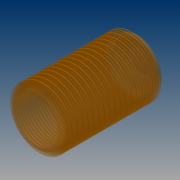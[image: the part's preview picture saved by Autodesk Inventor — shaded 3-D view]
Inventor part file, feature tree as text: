
AUTODESK INVENTOR PART (.ipt)
format: ipt  version: 2015 (Build 190159000, 159)  size: 459,264 bytes
history: native  units: mm
features: revolve x1, sketch x1
ambient origin geometry x8: Origin, YZ Plane, XZ Plane, XY Plane, X Axis, Y Axis, Z Axis, Center Point
bodies: Solid1 (feature_tree)
feature tree (2):
  revolve  "Revolution1"  [1 undecoded]
  sketch  "Sketch1"  dims[d34=40.0mm d36=20.0mm d37=10.0mm d38=5.0mm d39=10.0mm d40=2.0mm d41=10.0mm d42=10.0mm d43=2.0mm d44=10.0mm d45=2.0mm d46=10.0mm d47=2.0mm d48=10.0mm d49=2.0mm d50=10.0mm d51=2.0mm d52=10.0mm d53=2.0mm d54=10.0mm d55=2.0mm d56=10.0mm d57=2.0mm d59=2.0mm d62=3.0mm d63=3.0mm d64=3.0mm d65=3.0mm d66=3.0mm d67=3.0mm d68=3.0mm d69=3.0mm d70=3.0mm d72=90.0deg d73=2.0mm d74=2.0mm d75=2.0mm d76=2.0mm d77=2.0mm d78=2.0mm d79=2.0mm d80=2.0mm d81=3.0mm d82=10.0mm d83=3.0mm d84=3.0mm d85=3.0mm d86=3.0mm d87=3.0mm d88=3.0mm d89=3.0mm d90=195.0mm d91=2.0mm d92=2.0mm d93=2.0mm d94=2.0mm d95=2.0mm d96=2.0mm d97=2.0mm d98=2.0mm d99=2.0mm d101=3.0mm d102=3.0mm d103=3.0mm d104=3.0mm d105=3.0mm d106=3.0mm d107=3.0mm d108=3.0mm d109=3.0mm d110=2.0mm d111=2.0mm d112=2.0mm d113=3.0mm d114=3.0mm d115=3.0mm d116=2.0mm d117=2.0mm d118=2.0mm d119=2.0mm d120=2.0mm d121=3.0mm d122=3.0mm d123=3.0mm d124=3.0mm d125=3.0mm]
note: 1 required parameter value undecoded (feature->parameter linkage not recoverable at this tier; creation-order binding heuristic only, values carry confidence <= 0.55)
